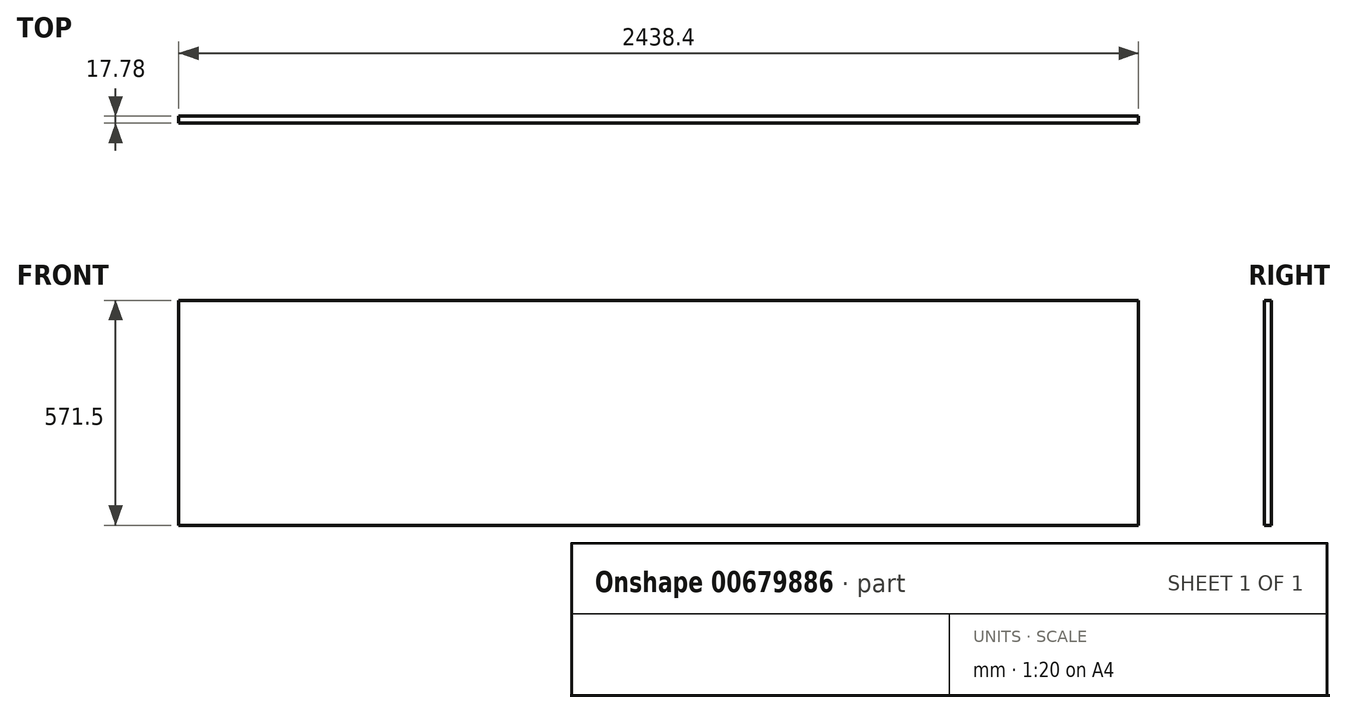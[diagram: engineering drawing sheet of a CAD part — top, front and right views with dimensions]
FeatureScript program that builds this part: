
annotation { "Feature Type Name" : "Feature", "Feature Type Description" : "" }
export const myFeature = defineFeature(function(context is Context, id is Id, definition is map)
    precondition{}
    {
        {
            var Q0;
            Q0=qCreatedBy(makeId("Front.planeOp"),FACE);
            var sketch = newSketch(context, id + "F0", { "sketchPlane" : qUnion([Q0])});
            skLineSegment(sketch, "E0.bottom", {"start": v(1219.2, 285.75) * mm, "end": v(-1219.2, 285.75) * mm});
            skLineSegment(sketch, "E0.top", {"start": v(1219.2, -285.75) * mm, "end": v(-1219.2, -285.75) * mm});
            skLineSegment(sketch, "E0.left", {"start": v(1219.2, 285.75) * mm, "end": v(1219.2, -285.75) * mm});
            skLineSegment(sketch, "E0.right", {"start": v(-1219.2, 285.75) * mm, "end": v(-1219.2, -285.75) * mm});
            skPoint(sketch, "E0.middle", {"position": v(0, 0) * mm});
            skSolve(sketch);
        }
        {
            var Q0;
            Q0=makeQuery(id+"F0.imprint","IMPRINT",FACE,{"disambiguationData":[TD([[makeQuery(id+"F0.imprint","IMPRINT",EDGE,{"derivedFrom":sQuery(id+"F0.wireOp",EDGE,"E0.bottom")}),1.0]])]});
            extrude(context, id + "F1", {"entities" : qUnion([Q0]), "endBound" : BoundingType.SYMMETRIC, "depth" : 17.78 * mm, "offsetDistance" : 25.4 * mm});
        }
    });
